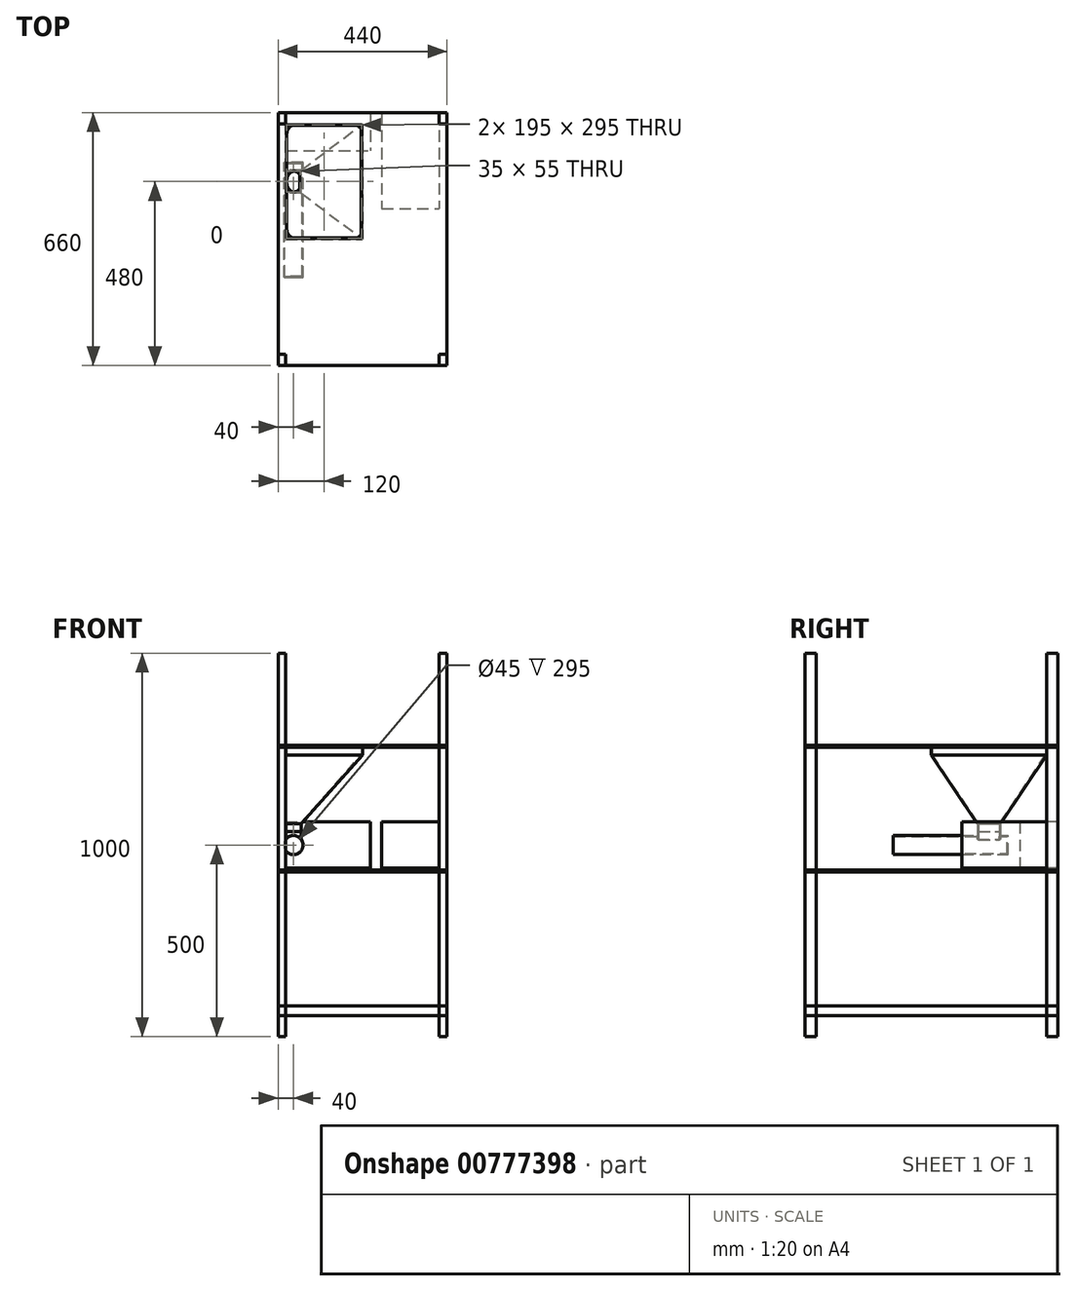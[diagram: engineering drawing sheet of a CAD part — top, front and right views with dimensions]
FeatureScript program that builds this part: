
annotation { "Feature Type Name" : "Feature", "Feature Type Description" : "" }
export const myFeature = defineFeature(function(context is Context, id is Id, definition is map)
    precondition{}
    {
        {
            var Q0;
            Q0=qCreatedBy(makeId("Front.planeOp"),FACE);
            var sketch = newSketch(context, id + "F0", { "sketchPlane" : qUnion([Q0])});
            skCircle(sketch, "E0", {"center": v(0, 0) * mm, "radius": 25 * mm});
            skSolve(sketch);
        }
        {
            var Q0;
            Q0 = qSketchRegion(id + "F0", true);
            extrude(context, id + "F1", {"entities" : qUnion([Q0]), "endBound" : BoundingType.SYMMETRIC, "depth" : 300 * mm, "offsetDistance" : 25 * mm});
        }
        {
            var Q0;
            Q0=qCreatedBy(makeId("Top.planeOp"),FACE);
            var sketch = newSketch(context, id + "F2", { "sketchPlane" : qUnion([Q0])});
            skLineSegment(sketch, "E1.bottom", {"start": v(20, 70) * mm, "end": v(-20, 70) * mm});
            skLineSegment(sketch, "E1.top", {"start": v(20, 130) * mm, "end": v(-20, 130) * mm});
            skLineSegment(sketch, "E1.left", {"start": v(20, 70) * mm, "end": v(20, 130) * mm});
            skLineSegment(sketch, "E1.right", {"start": v(-20, 70) * mm, "end": v(-20, 130) * mm});
            skPoint(sketch, "E1.middle", {"position": v(0, 100) * mm});
            skSolve(sketch);
        }
        {
            var Q0;
            Q0 = qSketchRegion(id + "F2", true);
            extrude(context, id + "F3", {"entities" : qUnion([Q0]), "operationType" : NewBodyOperationType.ADD, "depth" : 35 * mm, "offsetDistance" : 25 * mm});
        }
        {
            var Q0;
            Q0=makeQuery(id+"F3.opExtrude","CAP_FACE",FACE,{"disambiguationData":[OSD([sQuery(id+"F2.wireOp",EDGE,"E1.bottom"),sQuery(id+"F2.wireOp",EDGE,"E1.top"),sQuery(id+"F2.wireOp",EDGE,"E1.left"),sQuery(id+"F2.wireOp",EDGE,"E1.right")])],"isStart":false});
            shell(context, id + "F4", {"entities" : qUnion([Q0]), "thickness" : 2.5 * mm});
        }
        {
            var Q0;
            Q0=makeQuery(id+"F3.opExtrude","CAP_FACE",FACE,{"disambiguationData":[OSD([sQuery(id+"F2.wireOp",EDGE,"E1.bottom"),sQuery(id+"F2.wireOp",EDGE,"E1.top"),sQuery(id+"F2.wireOp",EDGE,"E1.left"),sQuery(id+"F2.wireOp",EDGE,"E1.right")])],"isStart":false});
            cPlane(context, id + "F5", {"entities" : qUnion([Q0]), "cplaneType" : CPlaneType.OFFSET, "offset" : 0 * mm, "width" : 150 * mm, "height" : 150 * mm});
        }
        {
            var Q0;
            Q0=qCreatedBy(id+"F5.planeOp",FACE);
            var sketch = newSketch(context, id + "F6", { "sketchPlane" : qUnion([Q0])});
            skLineSegment(sketch, "E2.0.0", {"start": v(20, 70) * mm, "end": v(20, 130) * mm});
            skLineSegment(sketch, "E2.0.1", {"start": v(20, 130) * mm, "end": v(-20, 130) * mm});
            skLineSegment(sketch, "E2.0.2", {"start": v(-20, 130) * mm, "end": v(-20, 70) * mm});
            skLineSegment(sketch, "E2.0.3", {"start": v(-20, 70) * mm, "end": v(20, 70) * mm});
            skSolve(sketch);
        }
        {
            var Q0;
            Q0 = qSketchRegion(id + "F6", true);
            extrude(context, id + "F7", {"entities" : qUnion([Q0]), "depth" : 20 * mm, "offsetDistance" : 25 * mm});
        }
        {
            var Q0;
            Q0=qCreatedBy(id+"F5.planeOp",FACE);
            cPlane(context, id + "F8", {"entities" : qUnion([Q0]), "cplaneType" : CPlaneType.OFFSET, "offset" : 200 * mm, "width" : 150 * mm, "height" : 150 * mm});
        }
        {
            var Q0;
            Q0=qCreatedBy(id+"F8.planeOp",FACE);
            var sketch = newSketch(context, id + "F9", { "sketchPlane" : qUnion([Q0])});
            skLineSegment(sketch, "E3.bottom", {"start": v(-20, 250) * mm, "end": v(180, 250) * mm});
            skLineSegment(sketch, "E3.top", {"start": v(-20, -50) * mm, "end": v(180, -50) * mm});
            skLineSegment(sketch, "E3.left", {"start": v(-20, 250) * mm, "end": v(-20, -50) * mm});
            skLineSegment(sketch, "E3.right", {"start": v(180, 250) * mm, "end": v(180, -50) * mm});
            skPoint(sketch, "E3.middle", {"position": v(80, 100) * mm});
            skLineSegment(sketch, "E4", {"start": v(202.68, 100) * mm, "end": v(-56.4, 100) * mm, "construction": true});
            skPoint(sketch, "E4.startSnap0", {"position": v(180, 100) * mm});
            skSolve(sketch);
        }
        {
            var Q0;
            Q0 = qSketchRegion(id + "F9", true);
            extrude(context, id + "F10", {"entities" : qUnion([Q0]), "depth" : 20 * mm, "offsetDistance" : 25 * mm});
        }
        {
            var Q0;
            Q0=makeQuery(id+"F7.opExtrude","CAP_FACE",FACE,{"disambiguationData":[OSD([sQuery(id+"F6.wireOp",EDGE,"E2.0.0"),sQuery(id+"F6.wireOp",EDGE,"E2.0.1"),sQuery(id+"F6.wireOp",EDGE,"E2.0.2"),sQuery(id+"F6.wireOp",EDGE,"E2.0.3")])],"isStart":false});
            var Q1;
            Q1=makeQuery(id+"F10.opExtrude","CAP_FACE",FACE,{"disambiguationData":[OSD([sQuery(id+"F9.wireOp",EDGE,"E3.bottom"),sQuery(id+"F9.wireOp",EDGE,"E3.top"),sQuery(id+"F9.wireOp",EDGE,"E3.left"),sQuery(id+"F9.wireOp",EDGE,"E3.right")])],"isStart":true});
            loft(context, id + "F11", {"sheetProfilesArray" : [{ "sheetProfileEntities" : qUnion([Q0]) }, { "sheetProfileEntities" : qUnion([Q1]) }]});
        }
        {
            var Q0;
            Q0=makeQuery(id+"F11.opLoft","CAP_FACE",FACE,{"disambiguationData":[OSD([sQuery(id+"F6.wireOp",EDGE,"E2.0.0"),sQuery(id+"F6.wireOp",EDGE,"E2.0.1"),sQuery(id+"F6.wireOp",EDGE,"E2.0.2"),sQuery(id+"F6.wireOp",EDGE,"E2.0.3")])],"isStart":true});
            var Q1;
            Q1=makeQuery(id+"F11.opLoft","CAP_FACE",FACE,{"disambiguationData":[OSD([sQuery(id+"F9.wireOp",EDGE,"E3.bottom"),sQuery(id+"F9.wireOp",EDGE,"E3.top"),sQuery(id+"F9.wireOp",EDGE,"E3.left"),sQuery(id+"F9.wireOp",EDGE,"E3.right")])],"isStart":true});
            var Q2;
            Q2=makeQuery(id+"F11.opLoft","SWEPT_BODY",BODY,{"disambiguationData":[OSD([sQuery(id+"F6.wireOp",EDGE,"E2.0.0"),sQuery(id+"F6.wireOp",EDGE,"E2.0.1"),sQuery(id+"F6.wireOp",EDGE,"E2.0.2"),sQuery(id+"F6.wireOp",EDGE,"E2.0.3"),sQuery(id+"F9.wireOp",EDGE,"E3.bottom"),sQuery(id+"F9.wireOp",EDGE,"E3.top"),sQuery(id+"F9.wireOp",EDGE,"E3.left"),sQuery(id+"F9.wireOp",EDGE,"E3.right")])]});
            shell(context, id + "F12", {"entities" : qUnion([Q0, Q1]), "parts" : qUnion([Q2]), "thickness" : 2.5 * mm});
        }
        {
            var Q0;
            Q0=makeQuery(id+"F12.opShell","OFFSET_EDGE",EDGE,{"disambiguationData":[OSD([sQuery(id+"F6.wireOp",EDGE,"E2.0.0"),sQuery(id+"F6.wireOp",EDGE,"E2.0.3"),sQuery(id+"F9.wireOp",EDGE,"E3.top"),sQuery(id+"F9.wireOp",EDGE,"E3.right")])]});
            var Q1;
            Q1=makeQuery(id+"F12.opShell","OFFSET_EDGE",EDGE,{"disambiguationData":[OSD([sQuery(id+"F6.wireOp",EDGE,"E2.0.2"),sQuery(id+"F6.wireOp",EDGE,"E2.0.3"),sQuery(id+"F9.wireOp",EDGE,"E3.top"),sQuery(id+"F9.wireOp",EDGE,"E3.left")])]});
            var Q2;
            Q2=makeQuery(id+"F12.opShell","OFFSET_EDGE",EDGE,{"disambiguationData":[OSD([sQuery(id+"F6.wireOp",EDGE,"E2.0.1"),sQuery(id+"F6.wireOp",EDGE,"E2.0.2"),sQuery(id+"F9.wireOp",EDGE,"E3.bottom"),sQuery(id+"F9.wireOp",EDGE,"E3.left")])]});
            var Q3;
            Q3=makeQuery(id+"F12.opShell","OFFSET_EDGE",EDGE,{"disambiguationData":[OSD([sQuery(id+"F6.wireOp",EDGE,"E2.0.0"),sQuery(id+"F6.wireOp",EDGE,"E2.0.1"),sQuery(id+"F9.wireOp",EDGE,"E3.bottom"),sQuery(id+"F9.wireOp",EDGE,"E3.right")])]});
            fillet(context, id + "F13", {"entities" : qUnion([Q0, Q1, Q2, Q3]), "radius" : 20 * mm, "tangentPropagation" : true, "allowEdgeOverflow" : false});
        }
        {
            var Q0;
            Q0=makeQuery(id+"F7.opExtrude","CAP_FACE",FACE,{"disambiguationData":[OSD([sQuery(id+"F6.wireOp",EDGE,"E2.0.0"),sQuery(id+"F6.wireOp",EDGE,"E2.0.1"),sQuery(id+"F6.wireOp",EDGE,"E2.0.2"),sQuery(id+"F6.wireOp",EDGE,"E2.0.3")])],"isStart":false});
            var Q1;
            Q1=makeQuery(id+"F7.opExtrude","CAP_FACE",FACE,{"disambiguationData":[OSD([sQuery(id+"F6.wireOp",EDGE,"E2.0.0"),sQuery(id+"F6.wireOp",EDGE,"E2.0.1"),sQuery(id+"F6.wireOp",EDGE,"E2.0.2"),sQuery(id+"F6.wireOp",EDGE,"E2.0.3")])],"isStart":true});
            shell(context, id + "F14", {"entities" : qUnion([Q0, Q1]), "thickness" : 2.5 * mm});
        }
        {
            var Q0;
            Q0=makeQuery(id+"F10.opExtrude","CAP_FACE",FACE,{"disambiguationData":[OSD([sQuery(id+"F9.wireOp",EDGE,"E3.bottom"),sQuery(id+"F9.wireOp",EDGE,"E3.top"),sQuery(id+"F9.wireOp",EDGE,"E3.left"),sQuery(id+"F9.wireOp",EDGE,"E3.right")])],"isStart":false});
            var Q1;
            Q1=makeQuery(id+"F10.opExtrude","CAP_FACE",FACE,{"disambiguationData":[OSD([sQuery(id+"F9.wireOp",EDGE,"E3.bottom"),sQuery(id+"F9.wireOp",EDGE,"E3.top"),sQuery(id+"F9.wireOp",EDGE,"E3.left"),sQuery(id+"F9.wireOp",EDGE,"E3.right")])],"isStart":true});
            shell(context, id + "F15", {"entities" : qUnion([Q0, Q1]), "thickness" : 2.5 * mm});
        }
        {
            var Q0;
            Q0=qCreatedBy(makeId("Top.planeOp"),FACE);
            var sketch = newSketch(context, id + "F16", { "sketchPlane" : qUnion([Q0])});
            skLineSegment(sketch, "E5.bottom", {"start": v(-20, 250) * mm, "end": v(-40, 250) * mm});
            skLineSegment(sketch, "E5.top", {"start": v(-20, 280) * mm, "end": v(-40, 280) * mm});
            skLineSegment(sketch, "E5.left", {"start": v(-20, 250) * mm, "end": v(-20, 280) * mm});
            skLineSegment(sketch, "E5.right", {"start": v(-40, 250) * mm, "end": v(-40, 280) * mm});
            skPoint(sketch, "E5.middle", {"position": v(-30, 265) * mm});
            skLineSegment(sketch, "E6.MirrorCS", {"start": v(380, 250) * mm, "end": v(400, 250) * mm});
            skLineSegment(sketch, "E7.MirrorCS", {"start": v(380, 280) * mm, "end": v(400, 280) * mm});
            skLineSegment(sketch, "E8.MirrorCS", {"start": v(380, 250) * mm, "end": v(380, 280) * mm});
            skLineSegment(sketch, "E9.MirrorCS", {"start": v(400, 250) * mm, "end": v(400, 280) * mm});
            skPoint(sketch, "E10.MirrorP", {"position": v(390, 265) * mm});
            skLineSegment(sketch, "E11.MirrorCS", {"start": v(-20, -380) * mm, "end": v(-40, -380) * mm});
            skLineSegment(sketch, "E12.MirrorCS", {"start": v(-20, -350) * mm, "end": v(-40, -350) * mm});
            skLineSegment(sketch, "E13.MirrorCS", {"start": v(-40, -350) * mm, "end": v(-40, -380) * mm});
            skLineSegment(sketch, "E14.MirrorCS", {"start": v(400, -350) * mm, "end": v(400, -380) * mm});
            skLineSegment(sketch, "E15.MirrorCS", {"start": v(380, -350) * mm, "end": v(380, -380) * mm});
            skLineSegment(sketch, "E16.MirrorCS", {"start": v(380, -380) * mm, "end": v(400, -380) * mm});
            skLineSegment(sketch, "E17.MirrorCS", {"start": v(-20, -350) * mm, "end": v(-20, -380) * mm});
            skLineSegment(sketch, "E18.MirrorCS", {"start": v(380, -350) * mm, "end": v(400, -350) * mm});
            skPoint(sketch, "E19.MirrorP", {"position": v(-30, -365) * mm});
            skPoint(sketch, "E20.MirrorP", {"position": v(390, -365) * mm});
            skSolve(sketch);
        }
        {
            var Q0;
            Q0 = qSketchRegion(id + "F16", true);
            extrude(context, id + "F17", {"entities" : qUnion([Q0]), "endBound" : BoundingType.SYMMETRIC, "depth" : 1000 * mm, "offsetDistance" : 25 * mm});
        }
        {
            var Q0;
            Q0=qCreatedBy(makeId("Top.planeOp"),FACE);
            cPlane(context, id + "F18", {"entities" : qUnion([Q0]), "cplaneType" : CPlaneType.OFFSET, "offset" : 70 * mm, "oppositeDirection" : true, "width" : 150 * mm, "height" : 150 * mm});
        }
        {
            var Q0;
            Q0=qCreatedBy(makeId("Top.planeOp"),FACE);
            var sketch = newSketch(context, id + "F19", { "sketchPlane" : qUnion([Q0])});
            skLineSegment(sketch, "E21.bottom", {"start": v(-20, 280) * mm, "end": v(200, 280) * mm});
            skLineSegment(sketch, "E21.top", {"start": v(-20, 180) * mm, "end": v(200, 180) * mm});
            skLineSegment(sketch, "E21.left", {"start": v(-20, 280) * mm, "end": v(-20, 180) * mm});
            skLineSegment(sketch, "E21.right", {"start": v(200, 280) * mm, "end": v(200, 180) * mm});
            skLineSegment(sketch, "E22", {"start": v(0, 86.99) * mm, "end": v(0, 382.57) * mm, "construction": true});
            skSolve(sketch);
        }
        {
            var Q0;
            Q0 = qSketchRegion(id + "F19", true);
            extrude(context, id + "F20", {"entities" : qUnion([Q0]), "endBound" : BoundingType.SYMMETRIC, "depth" : 120 * mm, "offsetDistance" : 25 * mm});
        }
        {
            var Q0;
            Q0=qCreatedBy(id+"F18.planeOp",FACE);
            var sketch = newSketch(context, id + "F21", { "sketchPlane" : qUnion([Q0])});
            skLineSegment(sketch, "E23.bottom", {"start": v(-40, 280) * mm, "end": v(400, 280) * mm});
            skLineSegment(sketch, "E23.top", {"start": v(-40, -380) * mm, "end": v(400, -380) * mm});
            skLineSegment(sketch, "E23.left", {"start": v(-40, 280) * mm, "end": v(-40, -380) * mm});
            skLineSegment(sketch, "E23.right", {"start": v(400, 280) * mm, "end": v(400, -380) * mm});
            skPoint(sketch, "E24.0.1.end.orphan", {"position": v(380, -380) * mm});
            skPoint(sketch, "E24.0.0.end.orphan", {"position": v(380, -350) * mm});
            skPoint(sketch, "E24.0.0.start.orphan", {"position": v(400, -350) * mm});
            skPoint(sketch, "E25.0.0.start.orphan", {"position": v(-20, 250) * mm});
            skPoint(sketch, "E25.0.1.start.orphan", {"position": v(-20, 280) * mm});
            skPoint(sketch, "E25.0.2.end.orphan", {"position": v(-40, 250) * mm});
            skSolve(sketch);
        }
        {
            var Q0;
            Q0 = qSketchRegion(id + "F21", true);
            extrude(context, id + "F22", {"entities" : qUnion([Q0]), "depth" : 5 * mm, "offsetDistance" : 25 * mm});
        }
        {
            var Q0;
            Q0=makeQuery(id+"F10.opExtrude","CAP_FACE",FACE,{"disambiguationData":[OSD([sQuery(id+"F9.wireOp",EDGE,"E3.bottom"),sQuery(id+"F9.wireOp",EDGE,"E3.top"),sQuery(id+"F9.wireOp",EDGE,"E3.left"),sQuery(id+"F9.wireOp",EDGE,"E3.right")])],"isStart":false});
            cPlane(context, id + "F23", {"entities" : qUnion([Q0]), "cplaneType" : CPlaneType.OFFSET, "offset" : 0 * mm, "width" : 150 * mm, "height" : 150 * mm});
        }
        {
            var Q0;
            Q0=qCreatedBy(id+"F23.planeOp",FACE);
            var sketch = newSketch(context, id + "F24", { "sketchPlane" : qUnion([Q0])});
            skPoint(sketch, "E26.0", {"position": v(-40, 280) * mm});
            skPoint(sketch, "E27.0", {"position": v(400, -380) * mm});
            skLineSegment(sketch, "E28.bottom", {"start": v(-40, 280) * mm, "end": v(400, 280) * mm});
            skLineSegment(sketch, "E28.top", {"start": v(-40, -380) * mm, "end": v(400, -380) * mm});
            skLineSegment(sketch, "E28.left", {"start": v(-40, 280) * mm, "end": v(-40, -380) * mm});
            skLineSegment(sketch, "E28.right", {"start": v(400, 280) * mm, "end": v(400, -380) * mm});
            skPoint(sketch, "E29.0", {"position": v(-17.5, 247.5) * mm});
            skPoint(sketch, "E30.0", {"position": v(177.5, -47.5) * mm});
            skLineSegment(sketch, "E31.bottom", {"start": v(-17.5, 247.5) * mm, "end": v(177.5, 247.5) * mm});
            skLineSegment(sketch, "E31.top", {"start": v(-17.5, -47.5) * mm, "end": v(177.5, -47.5) * mm});
            skLineSegment(sketch, "E31.left", {"start": v(-17.5, 247.5) * mm, "end": v(-17.5, -47.5) * mm});
            skLineSegment(sketch, "E31.right", {"start": v(177.5, 247.5) * mm, "end": v(177.5, -47.5) * mm});
            skSolve(sketch);
        }
        {
            var Q0;
            Q0 = qSketchRegion(id + "F24", true);
            extrude(context, id + "F25", {"entities" : qUnion([Q0]), "depth" : 5 * mm, "offsetDistance" : 25 * mm});
        }
        {
            var Q0;
            Q0=qCreatedBy(makeId("Top.planeOp"),FACE);
            var sketch = newSketch(context, id + "F26", { "sketchPlane" : qUnion([Q0])});
            skLineSegment(sketch, "E32.bottom", {"start": v(230, 280) * mm, "end": v(380, 280) * mm});
            skLineSegment(sketch, "E32.top", {"start": v(230, 30) * mm, "end": v(380, 30) * mm});
            skLineSegment(sketch, "E32.left", {"start": v(230, 280) * mm, "end": v(230, 30) * mm});
            skLineSegment(sketch, "E32.right", {"start": v(380, 280) * mm, "end": v(380, 30) * mm});
            skPoint(sketch, "E33.0", {"position": v(400, 280) * mm});
            skPoint(sketch, "E34.0", {"position": v(380, 280) * mm});
            skPoint(sketch, "E35.0", {"position": v(380, 250) * mm});
            skPoint(sketch, "E36.0", {"position": v(400, 250) * mm});
            skSolve(sketch);
        }
        {
            var Q0;
            Q0 = qSketchRegion(id + "F26", true);
            extrude(context, id + "F27", {"entities" : qUnion([Q0]), "endBound" : BoundingType.SYMMETRIC, "depth" : 120 * mm, "offsetDistance" : 25 * mm});
        }
        {
            var Q0;
            Q0=makeQuery(id+"F22.opExtrude","CAP_FACE",FACE,{"disambiguationData":[OSD([sQuery(id+"F21.wireOp",EDGE,"E23.bottom"),sQuery(id+"F21.wireOp",EDGE,"E23.top"),sQuery(id+"F21.wireOp",EDGE,"E23.left"),sQuery(id+"F21.wireOp",EDGE,"E23.right")])],"isStart":true});
            cPlane(context, id + "F28", {"entities" : qUnion([Q0]), "cplaneType" : CPlaneType.OFFSET, "offset" : 350 * mm, "width" : 150 * mm, "height" : 150 * mm});
        }
        {
            var Q0;
            Q0=qCreatedBy(id+"F28.planeOp",FACE);
            var sketch = newSketch(context, id + "F29", { "sketchPlane" : qUnion([Q0])});
            skPoint(sketch, "E37.0", {"position": v(-40, -280) * mm});
            skPoint(sketch, "E38.0", {"position": v(400, 380) * mm});
            skLineSegment(sketch, "E39.bottom", {"start": v(-40, -280) * mm, "end": v(400, -280) * mm});
            skLineSegment(sketch, "E39.top", {"start": v(-40, 380) * mm, "end": v(400, 380) * mm});
            skLineSegment(sketch, "E39.left", {"start": v(-40, -280) * mm, "end": v(-40, 380) * mm});
            skLineSegment(sketch, "E39.right", {"start": v(400, -280) * mm, "end": v(400, 380) * mm});
            skSolve(sketch);
        }
        {
            var Q0;
            Q0 = qSketchRegion(id + "F29", true);
            extrude(context, id + "F30", {"entities" : qUnion([Q0]), "depth" : 25 * mm, "offsetDistance" : 25 * mm});
        }
    });
